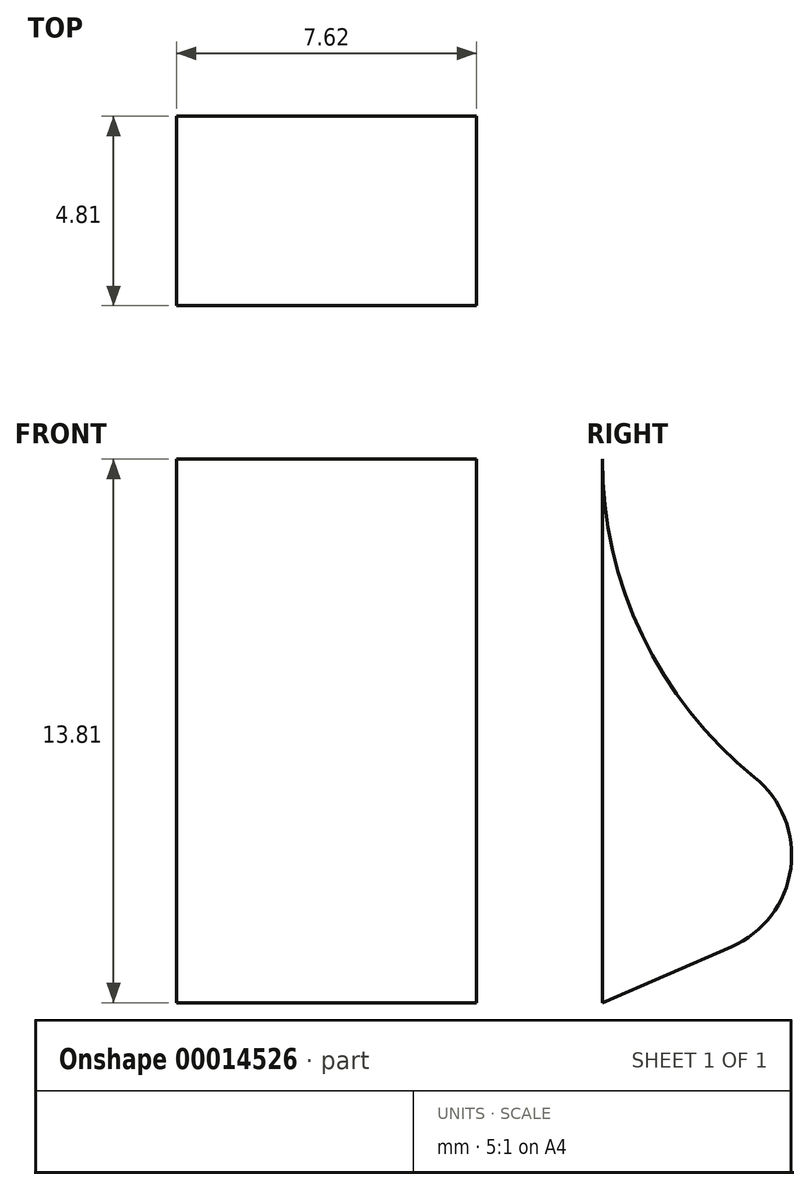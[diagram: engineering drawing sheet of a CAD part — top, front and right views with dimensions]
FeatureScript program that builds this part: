
annotation { "Feature Type Name" : "Feature", "Feature Type Description" : "" }
export const myFeature = defineFeature(function(context is Context, id is Id, definition is map)
    precondition{}
    {
        {
            var Q0;
            Q0=qCreatedBy(makeId("Right.planeOp"),FACE);
            var sketch = newSketch(context, id + "F0", { "sketchPlane" : qUnion([Q0])});
            skLineSegment(sketch, "E0", {"start": v(-43.53, 35.96) * mm, "end": v(-43.53, 22.15) * mm});
            skLineSegment(sketch, "E1", {"start": v(-43.53, 22.15) * mm, "end": v(-35.16, 25.77) * mm});
            skArc(sketch, "E2", {"start": v(-43.53, 35.96) * mm, "mid": v(-41.17, 29.37) * mm, "end": v(-35.16, 25.77) * mm});
            skSolve(sketch);
        }
        {
            var Q0;
            Q0 = qSketchRegion(id + "F0", true);
            extrude(context, id + "F1", {"entities" : qUnion([Q0]), "depth" : 7.62 * mm});
        }
        {
            var Q0;
            Q0=makeQuery(id+"F1.opExtrude","SWEPT_EDGE",EDGE,{"disambiguationData":[OSD([sQuery(id+"F0.wireOp",EDGE,"E1"),sQuery(id+"F0.wireOp",EDGE,"E2")])]});
            fillet(context, id + "F2", {"entities" : qUnion([Q0]), "radius" : 2.54 * mm, "tangentPropagation" : true, "allowEdgeOverflow" : false});
        }
    });
